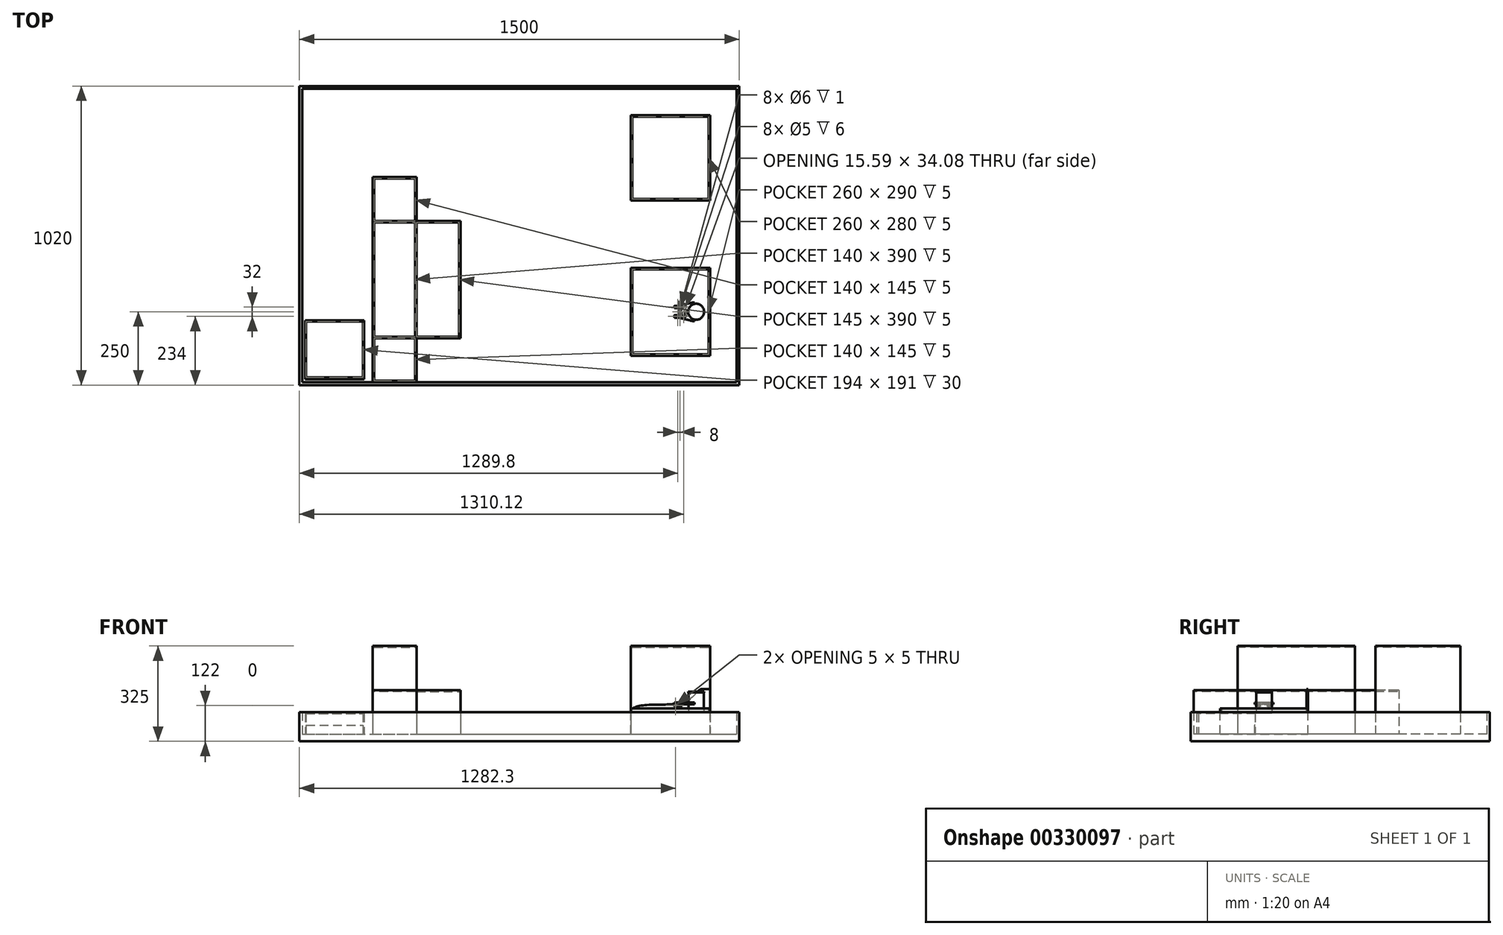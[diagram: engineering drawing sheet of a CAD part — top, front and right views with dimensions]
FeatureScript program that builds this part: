
annotation { "Feature Type Name" : "Feature", "Feature Type Description" : "" }
export const myFeature = defineFeature(function(context is Context, id is Id, definition is map)
    precondition{}
    {
        {
            var Q0;
            Q0=qCreatedBy(makeId("Top.planeOp"),FACE);
            var sketch = newSketch(context, id + "F0", { "sketchPlane" : qUnion([Q0])});
            skCircle(sketch, "E0", {"center": v(0, 0) * mm, "radius": 27.2 * mm});
            skSolve(sketch);
        }
        {
            var Q0;
            Q0=qSketchRegion(id+"F0",true);
            extrude(context, id + "F1", {"entities" : qUnion([Q0]), "depth" : 2.83 * mm});
        }
        {
            var Q0;
            Q0=makeQuery(id+"F1.opExtrude","CAP_FACE",FACE,{"disambiguationData":[OSD([sQuery(id+"F0.wireOp",EDGE,"E0")])],"isStart":false});
            var sketch = newSketch(context, id + "F2", { "sketchPlane" : qUnion([Q0])});
            skCircle(sketch, "E1", {"center": v(0, 0) * mm, "radius": 26.4 * mm});
            skSolve(sketch);
        }
        {
            var Q0;
            Q0=qSketchRegion(id+"F2",true);
            extrude(context, id + "F3", {"entities" : qUnion([Q0]), "operationType" : NewBodyOperationType.ADD, "depth" : 67.36 * mm});
        }
        {
            var Q0;
            Q0=makeQuery(id+"F3.opExtrude","CAP_FACE",FACE,{"disambiguationData":[OSD([sQuery(id+"F2.wireOp",EDGE,"E1")])],"isStart":false});
            var sketch = newSketch(context, id + "F4", { "sketchPlane" : qUnion([Q0])});
            skCircle(sketch, "E2", {"center": v(0, 0) * mm, "radius": 27.2 * mm});
            skSolve(sketch);
        }
        {
            var Q0;
            Q0=qSketchRegion(id+"F4",true);
            extrude(context, id + "F5", {"entities" : qUnion([Q0]), "operationType" : NewBodyOperationType.ADD, "depth" : 2.83 * mm});
        }
        {
            var Q0;
            Q0=makeQuery(id+"F5.opExtrude","CAP_FACE",FACE,{"disambiguationData":[OSD([sQuery(id+"F4.wireOp",EDGE,"E2")])],"isStart":false});
            var sketch = newSketch(context, id + "F6", { "sketchPlane" : qUnion([Q0])});
            skSolve(sketch);
        }
        {
            var Q0;
            Q0=qCreatedBy(makeId("Top.planeOp"),FACE);
            cPlane(context, id + "F7", {"entities" : qUnion([Q0]), "cplaneType" : CPlaneType.OFFSET, "offset" : 25 * mm, "width" : 150 * mm, "height" : 150 * mm});
        }
        {
            var Q0;
            Q0=makeQuery(id+"F6.imprint","IMPRINT",FACE,{"disambiguationData":[TD([[makeQuery(id+"F6.imprint","IMPRINT",EDGE,{"derivedFrom":makeQuery(id+"F5.opExtrude","CAP_EDGE",EDGE,{"disambiguationData":[OSD([sQuery(id+"F4.wireOp",EDGE,"E2")])],"isStart":false})}),1.0]])]});
            var sketch = newSketch(context, id + "F8", { "sketchPlane" : qUnion([Q0])});
            skSolve(sketch);
        }
        {
            var Q0;
            Q0=qCreatedBy(makeId("Top.planeOp"),FACE);
            var sketch = newSketch(context, id + "F9", { "sketchPlane" : qUnion([Q0])});
            skLineSegment(sketch, "E3.bottom", {"start": v(-222.8, -150) * mm, "end": v(47.2, -150) * mm});
            skLineSegment(sketch, "E3.top", {"start": v(-222.8, 150) * mm, "end": v(47.2, 150) * mm});
            skLineSegment(sketch, "E3.left", {"start": v(-222.8, -150) * mm, "end": v(-222.8, 150) * mm});
            skLineSegment(sketch, "E3.right", {"start": v(47.2, -150) * mm, "end": v(47.2, 150) * mm});
            skSolve(sketch);
        }
        {
            var Q0;
            Q0=qSketchRegion(id+"F9",true);
            extrude(context, id + "F10", {"entities" : qUnion([Q0]), "oppositeDirection" : true, "depth" : 72 * mm});
        }
        {
            var Q0;
            Q0=makeQuery(id+"F10.opExtrude","CAP_FACE",FACE,{"disambiguationData":[OSD([sQuery(id+"F9.wireOp",EDGE,"E3.bottom"),sQuery(id+"F9.wireOp",EDGE,"E3.top"),sQuery(id+"F9.wireOp",EDGE,"E3.left"),sQuery(id+"F9.wireOp",EDGE,"E3.right")])],"isStart":true});
            var sketch = newSketch(context, id + "F11", { "sketchPlane" : qUnion([Q0])});
            skLineSegment(sketch, "E4.bottom", {"start": v(-222.8, -150) * mm, "end": v(47.2, -150) * mm});
            skLineSegment(sketch, "E4.top", {"start": v(-222.8, -145) * mm, "end": v(42.2, -145) * mm});
            skLineSegment(sketch, "E4.left", {"start": v(-222.8, -150) * mm, "end": v(-222.8, -145) * mm});
            skLineSegment(sketch, "E5.bottom", {"start": v(47.2, 150) * mm, "end": v(42.2, 150) * mm});
            skLineSegment(sketch, "E5.left", {"start": v(47.2, 150) * mm, "end": v(47.2, -150) * mm});
            skLineSegment(sketch, "E5.right", {"start": v(42.2, 150) * mm, "end": v(42.2, -145) * mm});
            skSolve(sketch);
        }
        {
            var Q0;
            Q0=qSketchRegion(id+"F11",true);
            extrude(context, id + "F12", {"entities" : qUnion([Q0]), "operationType" : NewBodyOperationType.ADD, "depth" : 15 * mm});
        }
        {
            var Q0;
            Q0=makeQuery(id+"F12.boolean.opBoolean","MERGE",FACE,{"derivedFrom":[makeQuery(id+"F10.opExtrude","SWEPT_FACE",FACE,{"disambiguationData":[OSD([sQuery(id+"F9.wireOp",EDGE,"E3.top")])]}),makeQuery(id+"F12.opExtrude","SWEPT_FACE",FACE,{"disambiguationData":[OSD([sQuery(id+"F11.wireOp",EDGE,"E5.bottom")])]})]});
            var sketch = newSketch(context, id + "F13", { "sketchPlane" : qUnion([Q0])});
            skLineSegment(sketch, "E6", {"start": v(-47.2, 81.36) * mm, "end": v(-21.31, 81.36) * mm});
            skFitSpline(sketch, "E7", {"points": [v(-21.31, 81.36) * mm, v(15.24, 52.01) * mm, v(114.14, 28.17) * mm, v(222.8, 0) * mm], "startDerivative": vector(181.02, 0.3) * mm, "endDerivative": vector(-1.73, -239.85) * mm});
            skLineSegment(sketch, "E8", {"start": v(-47.2, 81.36) * mm, "end": v(-47.2, -72) * mm});
            skLineSegment(sketch, "E9", {"start": v(-47.2, -72) * mm, "end": v(222.8, -72) * mm});
            skLineSegment(sketch, "E10", {"start": v(222.8, -72) * mm, "end": v(222.8, 0) * mm});
            skSolve(sketch);
        }
        {
            var Q0;
            Q0=qSketchRegion(id+"F13",true);
            extrude(context, id + "F14", {"entities" : qUnion([Q0]), "operationType" : NewBodyOperationType.ADD, "oppositeDirection" : true, "depth" : 5 * mm});
        }
        {
            var Q0;
            Q0=makeQuery(id+"F10.opExtrude","CAP_FACE",FACE,{"disambiguationData":[OSD([sQuery(id+"F9.wireOp",EDGE,"E3.bottom"),sQuery(id+"F9.wireOp",EDGE,"E3.top"),sQuery(id+"F9.wireOp",EDGE,"E3.left"),sQuery(id+"F9.wireOp",EDGE,"E3.right")])],"isStart":true});
            var sketch = newSketch(context, id + "F15", { "sketchPlane" : qUnion([Q0])});
            skLineSegment(sketch, "E11.bottom", {"start": v(-222.8, 145) * mm, "end": v(-217.8, 145) * mm});
            skLineSegment(sketch, "E11.top", {"start": v(-222.8, -145) * mm, "end": v(-217.8, -145) * mm});
            skLineSegment(sketch, "E11.left", {"start": v(-222.8, 145) * mm, "end": v(-222.8, -145) * mm});
            skLineSegment(sketch, "E11.right", {"start": v(-217.8, 145) * mm, "end": v(-217.8, -145) * mm});
            skSolve(sketch);
        }
        {
            var Q0;
            Q0=qSketchRegion(id+"F15",true);
            extrude(context, id + "F16", {"entities" : qUnion([Q0]), "operationType" : NewBodyOperationType.ADD, "depth" : 5 * mm});
        }
        {
            var Q0;
            Q0=makeQuery(id+"F10.opExtrude","CAP_FACE",FACE,{"disambiguationData":[OSD([sQuery(id+"F9.wireOp",EDGE,"E3.bottom"),sQuery(id+"F9.wireOp",EDGE,"E3.top"),sQuery(id+"F9.wireOp",EDGE,"E3.left"),sQuery(id+"F9.wireOp",EDGE,"E3.right")])],"isStart":false});
            var sketch = newSketch(context, id + "F17", { "sketchPlane" : qUnion([Q0])});
            skLineSegment(sketch, "E12.bottom", {"start": v(147.2, 250) * mm, "end": v(-1352.8, 250) * mm});
            skLineSegment(sketch, "E12.top", {"start": v(147.2, -770) * mm, "end": v(-1352.8, -770) * mm});
            skLineSegment(sketch, "E12.left", {"start": v(147.2, 250) * mm, "end": v(147.2, -770) * mm});
            skLineSegment(sketch, "E12.right", {"start": v(-1352.8, 250) * mm, "end": v(-1352.8, -770) * mm});
            skSolve(sketch);
        }
        {
            var Q0;
            Q0=qSketchRegion(id+"F17",true);
            extrude(context, id + "F18", {"entities" : qUnion([Q0]), "operationType" : NewBodyOperationType.ADD, "depth" : 25 * mm});
        }
        {
            var Q0;
            Q0=makeQuery(id+"F18.opExtrude","CAP_FACE",FACE,{"disambiguationData":[OSD([sQuery(id+"F17.wireOp",EDGE,"E12.bottom"),sQuery(id+"F17.wireOp",EDGE,"E12.top"),sQuery(id+"F17.wireOp",EDGE,"E12.left"),sQuery(id+"F17.wireOp",EDGE,"E12.right")])],"isStart":true});
            var sketch = newSketch(context, id + "F19", { "sketchPlane" : qUnion([Q0])});
            skLineSegment(sketch, "E13.bottom", {"start": v(-222.8, 670) * mm, "end": v(47.2, 670) * mm});
            skLineSegment(sketch, "E13.top", {"start": v(-222.8, 380) * mm, "end": v(47.2, 380) * mm});
            skLineSegment(sketch, "E13.left", {"start": v(-222.8, 670) * mm, "end": v(-222.8, 380) * mm});
            skLineSegment(sketch, "E13.right", {"start": v(47.2, 670) * mm, "end": v(47.2, 380) * mm});
            skSolve(sketch);
        }
        {
            var Q0;
            Q0=qSketchRegion(id+"F19",true);
            extrude(context, id + "F20", {"entities" : qUnion([Q0]), "operationType" : NewBodyOperationType.ADD, "depth" : 300 * mm});
        }
        {
            var Q0;
            Q0=makeQuery(id+"F20.opExtrude","CAP_FACE",FACE,{"disambiguationData":[OSD([sQuery(id+"F19.wireOp",EDGE,"E13.bottom"),sQuery(id+"F19.wireOp",EDGE,"E13.top"),sQuery(id+"F19.wireOp",EDGE,"E13.left"),sQuery(id+"F19.wireOp",EDGE,"E13.right")])],"isStart":false});
            var sketch = newSketch(context, id + "F21", { "sketchPlane" : qUnion([Q0])});
            skLineSegment(sketch, "E14.bottom", {"start": v(-217.8, 665) * mm, "end": v(42.2, 665) * mm});
            skLineSegment(sketch, "E14.top", {"start": v(-217.8, 385) * mm, "end": v(42.2, 385) * mm});
            skLineSegment(sketch, "E14.left", {"start": v(-217.8, 665) * mm, "end": v(-217.8, 385) * mm});
            skLineSegment(sketch, "E14.right", {"start": v(42.2, 665) * mm, "end": v(42.2, 385) * mm});
            skSolve(sketch);
        }
        {
            var Q0;
            Q0=qSketchRegion(id+"F21",true);
            extrude(context, id + "F22", {"entities" : qUnion([Q0]), "operationType" : NewBodyOperationType.REMOVE, "oppositeDirection" : true, "depth" : 5 * mm});
        }
        {
            var Q0;
            Q0=makeQuery(id+"F18.opExtrude","CAP_FACE",FACE,{"disambiguationData":[OSD([sQuery(id+"F17.wireOp",EDGE,"E12.bottom"),sQuery(id+"F17.wireOp",EDGE,"E12.top"),sQuery(id+"F17.wireOp",EDGE,"E12.left"),sQuery(id+"F17.wireOp",EDGE,"E12.right")])],"isStart":true});
            var sketch = newSketch(context, id + "F23", { "sketchPlane" : qUnion([Q0])});
            skLineSegment(sketch, "E15.bottom", {"start": v(-1352.8, 770) * mm, "end": v(147.2, 770) * mm});
            skLineSegment(sketch, "E15.top", {"start": v(-1352.8, -250) * mm, "end": v(147.2, -250) * mm});
            skLineSegment(sketch, "E15.left", {"start": v(-1352.8, 770) * mm, "end": v(-1352.8, -250) * mm});
            skLineSegment(sketch, "E15.right", {"start": v(147.2, 770) * mm, "end": v(147.2, -250) * mm});
            skLineSegment(sketch, "E16.bottom", {"start": v(-1342.8, 760) * mm, "end": v(137.2, 760) * mm});
            skLineSegment(sketch, "E16.top", {"start": v(-1342.8, -240) * mm, "end": v(137.2, -240) * mm});
            skLineSegment(sketch, "E16.left", {"start": v(-1342.8, 760) * mm, "end": v(-1342.8, -240) * mm});
            skLineSegment(sketch, "E16.right", {"start": v(137.2, 760) * mm, "end": v(137.2, -240) * mm});
            skSolve(sketch);
        }
        {
            var Q0;
            Q0=qSketchRegion(id+"F23",true);
            extrude(context, id + "F24", {"entities" : qUnion([Q0]), "operationType" : NewBodyOperationType.ADD, "depth" : 75 * mm});
        }
        {
            var Q0;
            Q0=makeQuery(id+"F18.opExtrude","CAP_FACE",FACE,{"disambiguationData":[OSD([sQuery(id+"F17.wireOp",EDGE,"E12.bottom"),sQuery(id+"F17.wireOp",EDGE,"E12.top"),sQuery(id+"F17.wireOp",EDGE,"E12.left"),sQuery(id+"F17.wireOp",EDGE,"E12.right")])],"isStart":true});
            var sketch = newSketch(context, id + "F25", { "sketchPlane" : qUnion([Q0])});
            skLineSegment(sketch, "E17.bottom", {"start": v(-1102.8, 460) * mm, "end": v(-952.8, 460) * mm});
            skLineSegment(sketch, "E17.top", {"start": v(-1102.8, -240) * mm, "end": v(-952.8, -240) * mm});
            skLineSegment(sketch, "E17.left", {"start": v(-1102.8, 460) * mm, "end": v(-1102.8, -240) * mm});
            skLineSegment(sketch, "E17.right", {"start": v(-952.8, 460) * mm, "end": v(-952.8, 310) * mm});
            skLineSegment(sketch, "E18.bottom", {"start": v(-952.8, 310) * mm, "end": v(-802.8, 310) * mm});
            skLineSegment(sketch, "E18.top", {"start": v(-952.8, -90) * mm, "end": v(-802.8, -90) * mm});
            skLineSegment(sketch, "E18.right", {"start": v(-802.8, 310) * mm, "end": v(-802.8, -90) * mm});
            skLineSegment(sketch, "E19.trimOffspring", {"start": v(-952.8, -90) * mm, "end": v(-952.8, -240) * mm});
            skSolve(sketch);
        }
        {
            var Q0;
            Q0=qSketchRegion(id+"F25",true);
            extrude(context, id + "F26", {"entities" : qUnion([Q0]), "operationType" : NewBodyOperationType.ADD, "depth" : 150 * mm});
        }
        {
            var Q0;
            Q0=makeQuery(id+"F26.opExtrude","CAP_FACE",FACE,{"disambiguationData":[OSD([sQuery(id+"F25.wireOp",EDGE,"E17.bottom"),sQuery(id+"F25.wireOp",EDGE,"E17.top"),sQuery(id+"F25.wireOp",EDGE,"E17.left"),sQuery(id+"F25.wireOp",EDGE,"E17.right"),sQuery(id+"F25.wireOp",EDGE,"E18.bottom"),sQuery(id+"F25.wireOp",EDGE,"E18.top"),sQuery(id+"F25.wireOp",EDGE,"E18.right"),sQuery(id+"F25.wireOp",EDGE,"E19.trimOffspring")])],"isStart":false});
            var sketch = newSketch(context, id + "F27", { "sketchPlane" : qUnion([Q0])});
            skLineSegment(sketch, "E20.bottom", {"start": v(-952.8, 310) * mm, "end": v(-1102.8, 310) * mm});
            skLineSegment(sketch, "E20.top", {"start": v(-952.8, -90) * mm, "end": v(-1102.8, -90) * mm});
            skLineSegment(sketch, "E20.left", {"start": v(-952.8, 310) * mm, "end": v(-952.8, -90) * mm});
            skLineSegment(sketch, "E20.right", {"start": v(-1102.8, 310) * mm, "end": v(-1102.8, -90) * mm});
            skSolve(sketch);
        }
        {
            var Q0;
            Q0=qSketchRegion(id+"F27",true);
            extrude(context, id + "F28", {"entities" : qUnion([Q0]), "operationType" : NewBodyOperationType.ADD, "depth" : 150 * mm});
        }
        {
            var Q0;
            Q0=makeQuery(id+"F28.opExtrude","CAP_FACE",FACE,{"disambiguationData":[OSD([sQuery(id+"F27.wireOp",EDGE,"E20.bottom"),sQuery(id+"F27.wireOp",EDGE,"E20.top"),sQuery(id+"F27.wireOp",EDGE,"E20.left"),sQuery(id+"F27.wireOp",EDGE,"E20.right")])],"isStart":false});
            var sketch = newSketch(context, id + "F29", { "sketchPlane" : qUnion([Q0])});
            skLineSegment(sketch, "E21.bottom", {"start": v(-1097.8, 305) * mm, "end": v(-957.8, 305) * mm});
            skLineSegment(sketch, "E21.top", {"start": v(-1097.8, -85) * mm, "end": v(-957.8, -85) * mm});
            skLineSegment(sketch, "E21.left", {"start": v(-1097.8, 305) * mm, "end": v(-1097.8, -85) * mm});
            skLineSegment(sketch, "E21.right", {"start": v(-957.8, 305) * mm, "end": v(-957.8, -85) * mm});
            skSolve(sketch);
        }
        {
            var Q0;
            Q0=qSketchRegion(id+"F29",true);
            extrude(context, id + "F30", {"entities" : qUnion([Q0]), "operationType" : NewBodyOperationType.REMOVE, "oppositeDirection" : true, "depth" : 5 * mm});
        }
        {
            var Q0;
            {var subQ0=sQuery(id+"F25.wireOp",EDGE,"E17.left");var subQ1=sQuery(id+"F25.wireOp",EDGE,"E18.bottom");var subQ2=sQuery(id+"F25.wireOp",EDGE,"E17.right");var subQ3=sQuery(id+"F25.wireOp",EDGE,"E17.bottom");var subQ4=makeQuery(id+"F26.opExtrude","CAP_FACE",FACE,{"disambiguationData":[OSD([subQ3,sQuery(id+"F25.wireOp",EDGE,"E17.top"),subQ0,subQ2,subQ1,sQuery(id+"F25.wireOp",EDGE,"E18.top"),sQuery(id+"F25.wireOp",EDGE,"E18.right"),sQuery(id+"F25.wireOp",EDGE,"E19.trimOffspring")])],"isStart":false});Q0=makeQuery(id+"F28.boolean.opBoolean","SPLIT",FACE,{"disambiguationData":[TD([makeQuery(id+"F26.opExtrude","SWEPT_FACE",FACE,{"disambiguationData":[OSD([subQ3])]})])],"derivedFrom":subQ4});}
            var sketch = newSketch(context, id + "F31", { "sketchPlane" : qUnion([Q0])});
            skLineSegment(sketch, "E22.bottom", {"start": v(-1097.8, 455) * mm, "end": v(-957.8, 455) * mm});
            skLineSegment(sketch, "E22.top", {"start": v(-1097.8, 310) * mm, "end": v(-957.8, 310) * mm});
            skLineSegment(sketch, "E22.left", {"start": v(-1097.8, 455) * mm, "end": v(-1097.8, 310) * mm});
            skLineSegment(sketch, "E22.right", {"start": v(-957.8, 455) * mm, "end": v(-957.8, 310) * mm});
            skLineSegment(sketch, "E23.bottom", {"start": v(-952.8, 305) * mm, "end": v(-807.8, 305) * mm});
            skLineSegment(sketch, "E23.top", {"start": v(-952.8, -85) * mm, "end": v(-807.8, -85) * mm});
            skLineSegment(sketch, "E23.left", {"start": v(-952.8, 305) * mm, "end": v(-952.8, -85) * mm});
            skLineSegment(sketch, "E23.right", {"start": v(-807.8, 305) * mm, "end": v(-807.8, -85) * mm});
            skLineSegment(sketch, "E24.bottom", {"start": v(-1097.8, -90) * mm, "end": v(-957.8, -90) * mm});
            skLineSegment(sketch, "E24.top", {"start": v(-1097.8, -235) * mm, "end": v(-957.8, -235) * mm});
            skLineSegment(sketch, "E24.left", {"start": v(-1097.8, -90) * mm, "end": v(-1097.8, -235) * mm});
            skLineSegment(sketch, "E24.right", {"start": v(-957.8, -90) * mm, "end": v(-957.8, -235) * mm});
            skSolve(sketch);
        }
        {
            var Q0;
            Q0=qSketchRegion(id+"F31",true);
            extrude(context, id + "F32", {"entities" : qUnion([Q0]), "operationType" : NewBodyOperationType.REMOVE, "oppositeDirection" : true, "depth" : 5 * mm});
        }
        {
            var Q0;
            Q0=qCreatedBy(id+"F7.planeOp",FACE);
            var sketch = newSketch(context, id + "F33", { "sketchPlane" : qUnion([Q0])});
            skLineSegment(sketch, "E25", {"start": v(0, 0) * mm, "end": v(-90, 0) * mm, "construction": true});
            skLineSegment(sketch, "E26.bottom", {"start": v(-74.5, -12) * mm, "end": v(-55, -12) * mm});
            skLineSegment(sketch, "E26.top", {"start": v(-74.5, -20) * mm, "end": v(-55, -20) * mm});
            skLineSegment(sketch, "E26.left", {"start": v(-74.5, -12) * mm, "end": v(-74.5, -13) * mm});
            skPoint(sketch, "E27.visualSharp", {"position": v(-51, -12) * mm});
            skPoint(sketch, "E28.visualSharp", {"position": v(-51, -20) * mm});
            skCircle(sketch, "E29", {"center": v(-55, -16) * mm, "radius": 3 * mm});
            skLineSegment(sketch, "E30", {"start": v(-59, -3.98) * mm, "end": v(-59, -18.08) * mm, "construction": true});
            skCircle(sketch, "E31.MirrorC", {"center": v(-63, -16) * mm, "radius": 3 * mm});
            skLineSegment(sketch, "E32.bottom", {"start": v(-74.5, -13) * mm, "end": v(-65.65, -13) * mm});
            skLineSegment(sketch, "E32.top", {"start": v(-74.5, -19) * mm, "end": v(-65.65, -19) * mm});
            skArc(sketch, "E33", {"start": v(-65.65, -13) * mm, "mid": v(-67, -16) * mm, "end": v(-65.65, -19) * mm});
            skLineSegment(sketch, "E34.trimOffspring", {"start": v(-74.5, -19) * mm, "end": v(-74.5, -20) * mm});
            skArc(sketch, "E35.trimOffspring", {"start": v(-55, -20) * mm, "mid": v(-51, -16) * mm, "end": v(-55, -12) * mm});
            skLineSegment(sketch, "E36.MirrorCS", {"start": v(-74.5, 12) * mm, "end": v(-74.5, 13) * mm});
            skLineSegment(sketch, "E37.MirrorCS", {"start": v(-74.5, 19) * mm, "end": v(-74.5, 20) * mm});
            skPoint(sketch, "E38.MirrorP", {"position": v(-51, 12) * mm});
            skLineSegment(sketch, "E39.MirrorCS", {"start": v(-74.5, 12) * mm, "end": v(-55, 12) * mm});
            skPoint(sketch, "E40.MirrorP", {"position": v(-51, 20) * mm});
            skArc(sketch, "E41.MirrorCS", {"start": v(-65.65, 13) * mm, "mid": v(-67, 16) * mm, "end": v(-65.65, 19) * mm});
            skArc(sketch, "E42.MirrorCS", {"start": v(-55, 20) * mm, "mid": v(-51, 16) * mm, "end": v(-55, 12) * mm});
            skLineSegment(sketch, "E43.MirrorCS", {"start": v(-74.5, 20) * mm, "end": v(-55, 20) * mm});
            skCircle(sketch, "E44.MirrorC", {"center": v(-55, 16) * mm, "radius": 3 * mm});
            skCircle(sketch, "E45.MirrorC", {"center": v(-63, 16) * mm, "radius": 3 * mm});
            skLineSegment(sketch, "E46.MirrorCS", {"start": v(-74.5, 19) * mm, "end": v(-65.65, 19) * mm});
            skLineSegment(sketch, "E47.MirrorCS", {"start": v(-74.5, 13) * mm, "end": v(-65.65, 13) * mm});
            skSolve(sketch);
        }
        {
            var Q0;
            Q0=qSketchRegion(id+"F33",true);
            var Q1;
            Q1=qSketchRegion(id+"F36",true);
            extrude(context, id + "F34", {"entities" : qUnion([Q0, Q1]), "endBound" : BoundingType.SYMMETRIC, "depth" : 8 * mm});
        }
        {
            var Q0;
            Q0=makeQuery(id+"F34.opExtrude","CAP_EDGE",EDGE,{"disambiguationData":[OSD([sQuery(id+"F33.wireOp",EDGE,"E34.trimOffspring")])],"isStart":false});
            var Q1;
            Q1=makeQuery(id+"F34.opExtrude","CAP_EDGE",EDGE,{"disambiguationData":[OSD([sQuery(id+"F33.wireOp",EDGE,"E26.left")])],"isStart":false});
            var Q2;
            Q2=makeQuery(id+"F34.opExtrude","CAP_EDGE",EDGE,{"disambiguationData":[OSD([sQuery(id+"F33.wireOp",EDGE,"E34.trimOffspring")])],"isStart":true});
            var Q3;
            Q3=makeQuery(id+"F34.opExtrude","CAP_EDGE",EDGE,{"disambiguationData":[OSD([sQuery(id+"F33.wireOp",EDGE,"E26.left")])],"isStart":true});
            var Q4;
            Q4=makeQuery(id+"F34.opExtrude","CAP_EDGE",EDGE,{"disambiguationData":[OSD([sQuery(id+"F33.wireOp",EDGE,"E36.MirrorCS")])],"isStart":false});
            var Q5;
            Q5=makeQuery(id+"F34.opExtrude","CAP_EDGE",EDGE,{"disambiguationData":[OSD([sQuery(id+"F33.wireOp",EDGE,"E37.MirrorCS")])],"isStart":false});
            var Q6;
            Q6=makeQuery(id+"F34.opExtrude","CAP_EDGE",EDGE,{"disambiguationData":[OSD([sQuery(id+"F33.wireOp",EDGE,"E37.MirrorCS")])],"isStart":true});
            var Q7;
            Q7=makeQuery(id+"F34.opExtrude","CAP_EDGE",EDGE,{"disambiguationData":[OSD([sQuery(id+"F33.wireOp",EDGE,"E36.MirrorCS")])],"isStart":true});
            fillet(context, id + "F35", {"entities" : qUnion([Q0, Q1, Q2, Q3, Q4, Q5, Q6, Q7]), "radius" : 4 * mm, "tangentPropagation" : true, "allowEdgeOverflow" : false});
        }
        {
            var Q0;
            Q0=makeQuery(id+"F34.opExtrude","SWEPT_FACE",FACE,{"disambiguationData":[OSD([sQuery(id+"F33.wireOp",EDGE,"E26.top")])]});
            var sketch = newSketch(context, id + "F36", { "sketchPlane" : qUnion([Q0])});
            skCircle(sketch, "E48", {"center": v(-70.5, 25) * mm, "radius": 3 * mm});
            skSolve(sketch);
        }
        {
            var Q0;
            Q0=qSketchRegion(id+"F36",true);
            var Q1;
            Q1=makeQuery(id+"F34.opExtrude","SWEPT_FACE",FACE,{"disambiguationData":[OSD([sQuery(id+"F33.wireOp",EDGE,"E26.bottom")])]});
            extrude(context, id + "F37", {"entities" : qUnion([Q0]), "operationType" : NewBodyOperationType.ADD, "endBound" : BoundingType.UP_TO_SURFACE, "oppositeDirection" : true, "endBoundEntityFace" : qUnion([Q1]), "depth" : 25 * mm});
        }
        {
            var Q0;
            Q0=makeQuery(id+"F34.opExtrude","SWEPT_FACE",FACE,{"disambiguationData":[OSD([sQuery(id+"F33.wireOp",EDGE,"E43.MirrorCS")])]});
            var sketch = newSketch(context, id + "F38", { "sketchPlane" : qUnion([Q0])});
            skCircle(sketch, "E49", {"center": v(70.5, 25) * mm, "radius": 3 * mm});
            skSolve(sketch);
        }
        {
            var Q0;
            Q0=qSketchRegion(id+"F38",true);
            var Q1;
            Q1=makeQuery(id+"F34.opExtrude","SWEPT_FACE",FACE,{"disambiguationData":[OSD([sQuery(id+"F33.wireOp",EDGE,"E39.MirrorCS")])]});
            extrude(context, id + "F39", {"entities" : qUnion([Q0]), "operationType" : NewBodyOperationType.ADD, "endBound" : BoundingType.UP_TO_SURFACE, "oppositeDirection" : true, "endBoundEntityFace" : qUnion([Q1]), "depth" : 25 * mm});
        }
        {
            var Q0;
            Q0=qCreatedBy(id+"F7.planeOp",FACE);
            var sketch = newSketch(context, id + "F40", { "sketchPlane" : qUnion([Q0])});
            skCircle(sketch, "E50", {"center": v(-55, 16) * mm, "radius": 3 * mm});
            skCircle(sketch, "E51", {"center": v(-63, 16) * mm, "radius": 2.5 * mm});
            skCircle(sketch, "E52", {"center": v(-63, 16) * mm, "radius": 3 * mm});
            skCircle(sketch, "E53", {"center": v(-55, 16) * mm, "radius": 2.5 * mm});
            skSolve(sketch);
        }
        {
            var Q0;
            Q0=qSketchRegion(id+"F40",true);
            extrude(context, id + "F41", {"entities" : qUnion([Q0]), "operationType" : NewBodyOperationType.ADD, "endBound" : BoundingType.SYMMETRIC, "depth" : 6 * mm});
        }
        {
            var Q0;
            Q0=qCreatedBy(id+"F7.planeOp",FACE);
            var sketch = newSketch(context, id + "F42", { "sketchPlane" : qUnion([Q0])});
            skCircle(sketch, "E54", {"center": v(-63, -16) * mm, "radius": 2.5 * mm});
            skCircle(sketch, "E55", {"center": v(-63, -16) * mm, "radius": 3 * mm});
            skCircle(sketch, "E56", {"center": v(-55, -16) * mm, "radius": 2.5 * mm});
            skCircle(sketch, "E57", {"center": v(-55, -16) * mm, "radius": 3 * mm});
            skSolve(sketch);
        }
        {
            var Q0;
            Q0=qSketchRegion(id+"F42",true);
            extrude(context, id + "F43", {"entities" : qUnion([Q0]), "operationType" : NewBodyOperationType.ADD, "endBound" : BoundingType.SYMMETRIC, "depth" : 6 * mm});
        }
        {
            var Q0;
            Q0=makeQuery(id+"F34.opExtrude","SWEPT_FACE",FACE,{"disambiguationData":[OSD([sQuery(id+"F33.wireOp",EDGE,"E43.MirrorCS")])]});
            var sketch = newSketch(context, id + "F44", { "sketchPlane" : qUnion([Q0])});
            skArc(sketch, "E58", {"start": v(71.5, 27.3) * mm, "mid": v(70.5, 27.5) * mm, "end": v(69.5, 27.3) * mm});
            skLineSegment(sketch, "E59.bottom", {"start": v(68.2, 26) * mm, "end": v(69.5, 26) * mm});
            skLineSegment(sketch, "E59.top", {"start": v(68.2, 24) * mm, "end": v(69.5, 24) * mm});
            skLineSegment(sketch, "E60.left", {"start": v(71.5, 27.3) * mm, "end": v(71.5, 26) * mm});
            skLineSegment(sketch, "E60.right", {"start": v(69.5, 27.3) * mm, "end": v(69.5, 26) * mm});
            skPoint(sketch, "E61.orphan", {"position": v(69.5, 27.8) * mm});
            skPoint(sketch, "E62.orphan", {"position": v(71.5, 27.8) * mm});
            skArc(sketch, "E63.trimOffspring", {"start": v(68.2, 26) * mm, "mid": v(68, 25) * mm, "end": v(68.2, 24) * mm});
            skPoint(sketch, "E59.left.start.orphan", {"position": v(67.32, 26) * mm});
            skPoint(sketch, "E64.orphan", {"position": v(67.32, 24) * mm});
            skArc(sketch, "E65.trimOffspring", {"start": v(69.5, 22.7) * mm, "mid": v(70.5, 22.5) * mm, "end": v(71.5, 22.7) * mm});
            skLineSegment(sketch, "E66.trimOffspring", {"start": v(69.5, 24) * mm, "end": v(69.5, 22.7) * mm});
            skLineSegment(sketch, "E67.trimOffspring", {"start": v(71.5, 26) * mm, "end": v(72.8, 26) * mm});
            skLineSegment(sketch, "E68.trimOffspring", {"start": v(71.5, 24) * mm, "end": v(71.5, 22.7) * mm});
            skLineSegment(sketch, "E69.trimOffspring", {"start": v(71.5, 24) * mm, "end": v(72.8, 24) * mm});
            skPoint(sketch, "E60.top.end.orphan", {"position": v(69.5, 22.2) * mm});
            skPoint(sketch, "E70.orphan", {"position": v(71.5, 22.2) * mm});
            skPoint(sketch, "E59.right.end.orphan", {"position": v(73.68, 24) * mm});
            skPoint(sketch, "E71.orphan", {"position": v(73.68, 26) * mm});
            skArc(sketch, "E72.trimOffspring", {"start": v(72.8, 24) * mm, "mid": v(73, 25) * mm, "end": v(72.8, 26) * mm});
            skSolve(sketch);
        }
        {
            var Q0;
            Q0=qSketchRegion(id+"F44",true);
            extrude(context, id + "F45", {"entities" : qUnion([Q0]), "operationType" : NewBodyOperationType.REMOVE, "endBound" : BoundingType.THROUGH_ALL, "oppositeDirection" : true, "depth" : 25 * mm});
        }
        {
            var Q0;
            Q0=makeQuery(id+"F18.opExtrude","CAP_FACE",FACE,{"disambiguationData":[OSD([sQuery(id+"F17.wireOp",EDGE,"E12.bottom"),sQuery(id+"F17.wireOp",EDGE,"E12.top"),sQuery(id+"F17.wireOp",EDGE,"E12.left"),sQuery(id+"F17.wireOp",EDGE,"E12.right")])],"isStart":true});
            var sketch = newSketch(context, id + "F46", { "sketchPlane" : qUnion([Q0])});
            skLineSegment(sketch, "E73.bottom", {"start": v(-1332.8, -30) * mm, "end": v(-1132.8, -30) * mm});
            skLineSegment(sketch, "E73.top", {"start": v(-1332.8, -230) * mm, "end": v(-1132.8, -230) * mm});
            skLineSegment(sketch, "E73.left", {"start": v(-1332.8, -30) * mm, "end": v(-1332.8, -230) * mm});
            skLineSegment(sketch, "E73.right", {"start": v(-1132.8, -30) * mm, "end": v(-1132.8, -230) * mm});
            skLineSegment(sketch, "E74.bottom", {"start": v(-1329.8, -33) * mm, "end": v(-1135.8, -33) * mm});
            skLineSegment(sketch, "E74.top", {"start": v(-1329.8, -224) * mm, "end": v(-1135.8, -224) * mm});
            skLineSegment(sketch, "E74.left", {"start": v(-1329.8, -33) * mm, "end": v(-1329.8, -224) * mm});
            skLineSegment(sketch, "E74.right", {"start": v(-1135.8, -33) * mm, "end": v(-1135.8, -224) * mm});
            skSolve(sketch);
        }
        {
            var Q0;
            Q0=qSketchRegion(id+"F46",true);
            extrude(context, id + "F47", {"entities" : qUnion([Q0]), "operationType" : NewBodyOperationType.ADD, "depth" : 30 * mm});
        }
        {
            var Q0;
            Q0=makeQuery(id+"F47.opExtrude","CAP_FACE",FACE,{"disambiguationData":[OSD([sQuery(id+"F46.wireOp",EDGE,"E73.bottom"),sQuery(id+"F46.wireOp",EDGE,"E73.top"),sQuery(id+"F46.wireOp",EDGE,"E73.left"),sQuery(id+"F46.wireOp",EDGE,"E73.right"),sQuery(id+"F46.wireOp",EDGE,"E74.bottom"),sQuery(id+"F46.wireOp",EDGE,"E74.top"),sQuery(id+"F46.wireOp",EDGE,"E74.left"),sQuery(id+"F46.wireOp",EDGE,"E74.right")])],"isStart":false});
            var sketch = newSketch(context, id + "F48", { "sketchPlane" : qUnion([Q0])});
            skLineSegment(sketch, "E75.bottom", {"start": v(-1332.8, -30) * mm, "end": v(-1329.8, -30) * mm});
            skLineSegment(sketch, "E75.top", {"start": v(-1332.8, -230) * mm, "end": v(-1329.8, -230) * mm});
            skLineSegment(sketch, "E75.left", {"start": v(-1332.8, -30) * mm, "end": v(-1332.8, -230) * mm});
            skLineSegment(sketch, "E75.right", {"start": v(-1329.8, -30) * mm, "end": v(-1329.8, -224) * mm});
            skLineSegment(sketch, "E76.bottom", {"start": v(-1329.8, -230) * mm, "end": v(-1135.8, -230) * mm});
            skLineSegment(sketch, "E76.top", {"start": v(-1329.8, -224) * mm, "end": v(-1135.8, -224) * mm});
            skLineSegment(sketch, "E77.bottom", {"start": v(-1135.8, -230) * mm, "end": v(-1132.8, -230) * mm});
            skLineSegment(sketch, "E77.top", {"start": v(-1135.8, -30) * mm, "end": v(-1132.8, -30) * mm});
            skLineSegment(sketch, "E77.left", {"start": v(-1135.8, -224) * mm, "end": v(-1135.8, -30) * mm});
            skLineSegment(sketch, "E77.right", {"start": v(-1132.8, -230) * mm, "end": v(-1132.8, -30) * mm});
            skSolve(sketch);
        }
        {
            var Q0;
            Q0=qSketchRegion(id+"F48",true);
            extrude(context, id + "F49", {"entities" : qUnion([Q0]), "operationType" : NewBodyOperationType.ADD, "depth" : 40 * mm});
        }
        {
            var Q0;
            Q0=makeQuery(id+"F34.opExtrude","CAP_FACE",FACE,{"disambiguationData":[OSD([sQuery(id+"F33.wireOp",EDGE,"E36.MirrorCS"),sQuery(id+"F33.wireOp",EDGE,"E37.MirrorCS"),sQuery(id+"F33.wireOp",EDGE,"E39.MirrorCS"),sQuery(id+"F33.wireOp",EDGE,"E41.MirrorCS"),sQuery(id+"F33.wireOp",EDGE,"E42.MirrorCS"),sQuery(id+"F33.wireOp",EDGE,"E43.MirrorCS"),sQuery(id+"F33.wireOp",EDGE,"E44.MirrorC"),sQuery(id+"F33.wireOp",EDGE,"E45.MirrorC"),sQuery(id+"F33.wireOp",EDGE,"E46.MirrorCS"),sQuery(id+"F33.wireOp",EDGE,"E47.MirrorCS")])],"isStart":false});
            var sketch = newSketch(context, id + "F50", { "sketchPlane" : qUnion([Q0])});
            skLineSegment(sketch, "E78.left", {"start": v(-74.23, 20) * mm, "end": v(-74.2, 12) * mm});
            skLineSegment(sketch, "E78.right", {"start": v(-5.48, 32) * mm, "end": v(-5.46, 26.65) * mm});
            skArc(sketch, "E79", {"start": v(-5.46, 26.65) * mm, "mid": v(-19.22, 19.25) * mm, "end": v(-26.64, 5.5) * mm});
            skCircle(sketch, "E80", {"center": v(-63, 16) * mm, "radius": 2.5 * mm});
            skCircle(sketch, "E81", {"center": v(-55, 16) * mm, "radius": 2.5 * mm});
            skLineSegment(sketch, "E82.bottom", {"start": v(-74.2, 12) * mm, "end": v(-54.39, 12) * mm});
            skLineSegment(sketch, "E82.right", {"start": v(-54.39, 12) * mm, "end": v(-54.39, 0) * mm});
            skFitSpline(sketch, "E83", {"points": [v(-74.23, 20) * mm, v(-5.48, 32) * mm], "startDerivative": vector(87.9, 1.5) * mm, "endDerivative": vector(43.82, 0) * mm});
            skPoint(sketch, "E84.orphan", {"position": v(-74.27, 28) * mm});
            skLineSegment(sketch, "E85", {"start": v(-31.6, 0) * mm, "end": v(-31.6, 6.1) * mm});
            skLineSegment(sketch, "E86", {"start": v(-31.6, 6.1) * mm, "end": v(-26.64, 5.5) * mm});
            skLineSegment(sketch, "E87", {"start": v(-78.25, 0) * mm, "end": v(-30.79, 0) * mm, "construction": true});
            skLineSegment(sketch, "E88.MirrorCS", {"start": v(-31.6, 0) * mm, "end": v(-31.6, -6.1) * mm});
            skLineSegment(sketch, "E89.MirrorCS", {"start": v(-31.6, -6.1) * mm, "end": v(-26.64, -5.5) * mm});
            skArc(sketch, "E90.MirrorCS", {"start": v(-5.46, -26.65) * mm, "mid": v(-19.22, -19.25) * mm, "end": v(-26.64, -5.5) * mm});
            skLineSegment(sketch, "E91.MirrorCS", {"start": v(-5.48, -32) * mm, "end": v(-5.46, -26.65) * mm});
            skFitSpline(sketch, "E92.MirrorCS", {"points": [v(-74.23, -20) * mm, v(-5.48, -32) * mm], "startDerivative": vector(87.9, -1.5) * mm, "endDerivative": vector(43.82, 0) * mm});
            skLineSegment(sketch, "E93.MirrorCS", {"start": v(-74.23, -20) * mm, "end": v(-74.2, -12) * mm});
            skLineSegment(sketch, "E94.MirrorCS", {"start": v(-74.2, -12) * mm, "end": v(-54.39, -12) * mm});
            skLineSegment(sketch, "E95.MirrorCS", {"start": v(-54.39, -12) * mm, "end": v(-54.39, 0) * mm});
            skCircle(sketch, "E96.MirrorC", {"center": v(-55, -16) * mm, "radius": 2.5 * mm});
            skCircle(sketch, "E97.MirrorC", {"center": v(-63, -16) * mm, "radius": 2.5 * mm});
            skFitSpline(sketch, "E98", {"points": [v(-49.27, 0) * mm, v(-49.11, 10.4) * mm, v(-35.54, 17.02) * mm, v(-41.2, 0) * mm], "startDerivative": vector(-12.08, 36.99) * mm, "endDerivative": vector(-33.41, -62.4) * mm});
            skFitSpline(sketch, "E99.MirrorCS", {"points": [v(-49.27, 0) * mm, v(-49.11, -10.4) * mm, v(-35.54, -17.02) * mm, v(-41.2, 0) * mm], "startDerivative": vector(-12.08, -36.99) * mm, "endDerivative": vector(-33.41, 62.4) * mm});
            skSolve(sketch);
        }
        {
            var Q0;
            Q0 = qSketchRegion(id + "F50", true);
            extrude(context, id + "F51", {"entities" : qUnion([Q0]), "depth" : 5 * mm});
        }
        {
            var Q0;
            Q0 = qSketchRegion(id + "F50", true);
            extrude(context, id + "F52", {"entities" : qUnion([Q0]), "operationType" : NewBodyOperationType.ADD, "depth" : 6 * mm});
        }
    });
